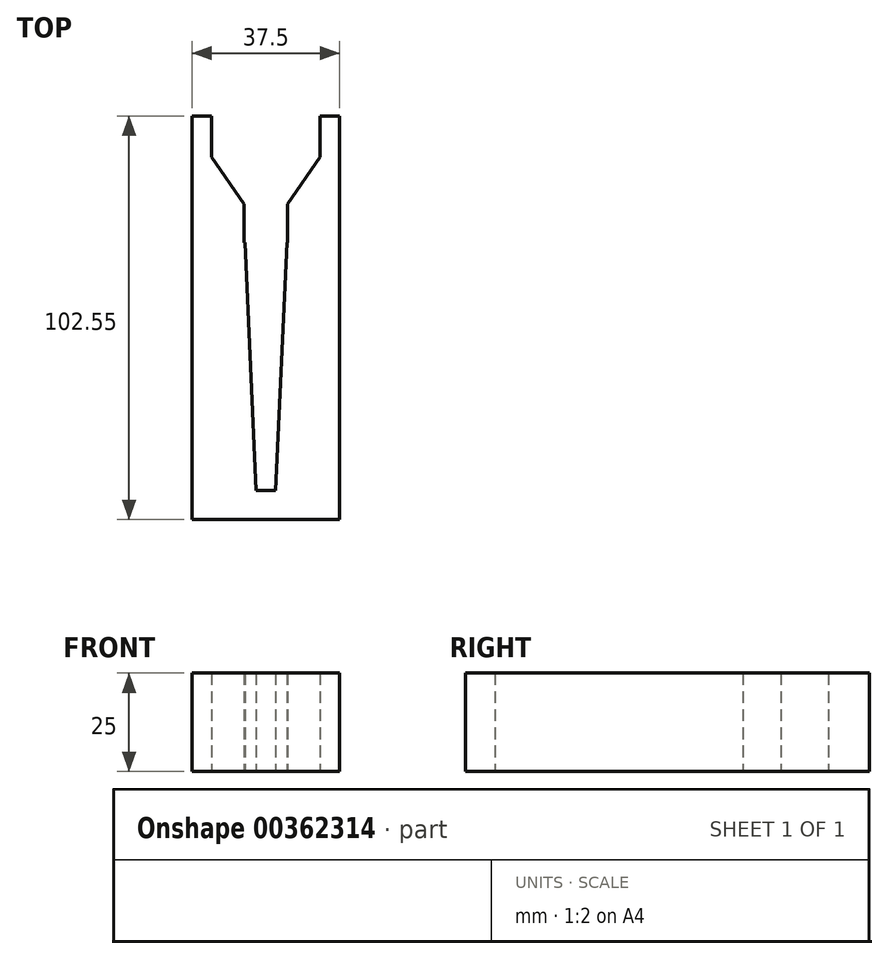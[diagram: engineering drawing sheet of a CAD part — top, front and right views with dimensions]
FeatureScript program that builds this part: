
annotation { "Feature Type Name" : "Feature", "Feature Type Description" : "" }
export const myFeature = defineFeature(function(context is Context, id is Id, definition is map)
    precondition{}
    {
        {
            var Q0;
            Q0=qCreatedBy(makeId("Top.planeOp"),FACE);
            var sketch = newSketch(context, id + "F0", { "sketchPlane" : qUnion([Q0])});
            skLineSegment(sketch, "E0", {"start": v(-2.5, -55.5) * mm, "end": v(-5.35, 7.5) * mm});
            skLineSegment(sketch, "E1", {"start": v(5.35, 7.5) * mm, "end": v(2.5, -55.5) * mm});
            skLineSegment(sketch, "E2", {"start": v(-5.35, 7.5) * mm, "end": v(5.35, 7.5) * mm, "construction": true});
            skLineSegment(sketch, "E3.top", {"start": v(5.5, 17.2) * mm, "end": v(-5.5, 17.2) * mm, "construction": true});
            skLineSegment(sketch, "E3.left", {"start": v(5.5, 7.5) * mm, "end": v(5.5, 17.2) * mm});
            skLineSegment(sketch, "E3.right", {"start": v(-5.5, 7.5) * mm, "end": v(-5.5, 17.2) * mm});
            skPoint(sketch, "E3.middle", {"position": v(0, 12.35) * mm});
            skPoint(sketch, "E3.middle.positionSnap0", {"position": v(0, 7.5) * mm});
            skPoint(sketch, "E3.centerSnap0", {"position": v(0, 7.5) * mm});
            skLineSegment(sketch, "E4", {"start": v(-5.5, 17.2) * mm, "end": v(-13.75, 29.2) * mm});
            skLineSegment(sketch, "E5", {"start": v(-13.75, 29.2) * mm, "end": v(-13.75, 39.64) * mm});
            skLineSegment(sketch, "E6", {"start": v(-13.75, 39.64) * mm, "end": v(13.75, 39.64) * mm, "construction": true});
            skLineSegment(sketch, "E7", {"start": v(13.75, 39.64) * mm, "end": v(13.75, 29.2) * mm});
            skLineSegment(sketch, "E8", {"start": v(13.75, 29.2) * mm, "end": v(5.5, 17.2) * mm});
            skLineSegment(sketch, "E9", {"start": v(-13.75, 39.64) * mm, "end": v(-18.75, 39.64) * mm});
            skLineSegment(sketch, "E10", {"start": v(-18.75, 39.64) * mm, "end": v(-18.75, -62.9) * mm});
            skLineSegment(sketch, "E11", {"start": v(-18.75, -62.9) * mm, "end": v(18.75, -62.9) * mm});
            skLineSegment(sketch, "E12", {"start": v(18.75, -62.9) * mm, "end": v(18.75, 39.64) * mm});
            skLineSegment(sketch, "E13", {"start": v(18.75, 39.64) * mm, "end": v(13.75, 39.64) * mm});
            skLineSegment(sketch, "E14", {"start": v(-5.35, 7.5) * mm, "end": v(-5.5, 7.5) * mm});
            skLineSegment(sketch, "E15", {"start": v(5.35, 7.5) * mm, "end": v(5.5, 7.5) * mm});
            skLineSegment(sketch, "E16", {"start": v(-2.5, -55.5) * mm, "end": v(2.5, -55.5) * mm});
            skSolve(sketch);
        }
        {
            var Q0;
            Q0 = qSketchRegion(id + "F0", true);
            extrude(context, id + "F1", {"entities" : qUnion([Q0]), "depth" : 25 * mm});
        }
    });
